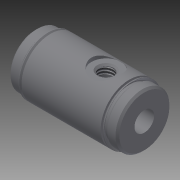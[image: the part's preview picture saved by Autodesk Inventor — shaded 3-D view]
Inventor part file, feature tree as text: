
AUTODESK INVENTOR PART (.ipt)
format: ipt  version: 2014 (Build 180170000, 170)  size: 206,336 bytes
history: native  units: in
note: dims shown in document units (in); Inventor stores cm internally (conversion verified against a paired STEP export)
features: other x49, sketch x5, revolve x4, hole x1, thread x1
ambient origin geometry x8: Origin, YZ Plane, XZ Plane, XY Plane, X Axis, Y Axis, Z Axis, Center Point
bodies: Solid1 (feature_tree)
feature tree (60):
  revolve  "Revolution1"  Angle=360.0deg
  hole  "Hole1"  [1 undecoded]
  revolve  "Revolution2"  [1 undecoded]
  thread  "Thread1"  [1 undecoded]
  revolve  "Revolution3"  [1 undecoded]
  revolve  "Revolution4"  [1 undecoded]
  other  "ba2_XY"
  other  "ba2_YZ"
  other  "ba2_ZX"
  other  "ba2_X"
  other  "ba2_Y"
  other  "ba2_Z"
  other  "ba2_Center"
  other  "centar_XY"
  other  "centar_YZ"
  other  "centar_ZX"
  other  "centar_X"
  other  "centar_Y"
  other  "centar_Z"
  other  "centar_Center"
  other  "d1_XY"
  other  "d1_YZ"
  other  "d1_ZX"
  other  "d1_X"
  other  "d1_Y"
  other  "d1_Z"
  other  "d1_Center"
  other  "d2_XY"
  other  "d2_YZ"
  other  "d2_ZX"
  other  "d2_X"
  other  "d2_Y"
  other  "d2_Z"
  other  "d2_Center"
  other  "to_cyl_A_XY"
  other  "to_cyl_A_YZ"
  other  "to_cyl_A_ZX"
  other  "to_cyl_A_X"
  other  "to_cyl_A_Y"
  other  "to_cyl_A_Z"
  other  "to_cyl_A_Center"
  other  "to_cyl_B_XY"
  other  "to_cyl_B_YZ"
  other  "to_cyl_B_ZX"
  other  "to_cyl_B_X"
  other  "to_cyl_B_Y"
  other  "to_cyl_B_Z"
  other  "to_cyl_B_Center"
  other  "to_rod_A_XY"
  other  "to_rod_A_YZ"
  other  "to_rod_A_ZX"
  other  "to_rod_A_X"
  other  "to_rod_A_Y"
  other  "to_rod_A_Z"
  other  "to_rod_A_Center"
  sketch  "Sketch_1"  dims[d0=360.0deg]
  sketch  "Sketch2"  dims[d1=0.21in d2=0.75in d3=0.375in d4=0.25in d5=0.5635in d6=1.156in d7=0.0in d8=360.0deg]
  sketch  "Sketch_6"  dims[d9=0.0955in d10=0.1018in d11=360.0deg]
  sketch  "Sketch_8"  dims[d12=360.0deg]
  sketch  "Sketch_14"
note: 5 required parameter values undecoded (feature->parameter linkage not recoverable at this tier; creation-order binding heuristic only, values carry confidence <= 0.55)
